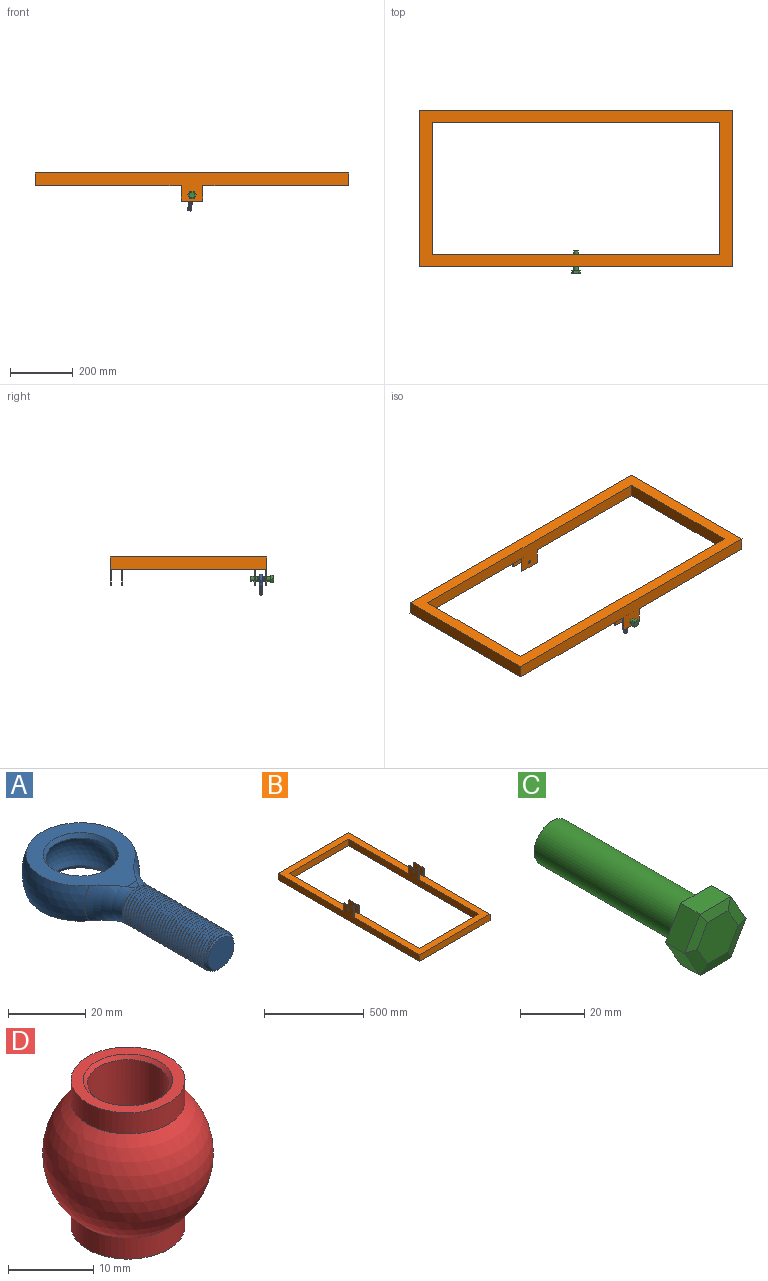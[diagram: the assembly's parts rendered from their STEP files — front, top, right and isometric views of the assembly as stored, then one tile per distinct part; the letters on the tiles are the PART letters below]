
ASSEMBLY  parts=4 mates=4
PART A: 18 faces, bbox 40.4x67.6x40.4 mm
  f0: sphere r=10mm, area 550.8mm2, adj f16,f17
  f1: sphere r=15.24mm, area 857.9mm2, adj f2,f6,f12,f14
  f2: torus R=18.29mm, axis (0,-1,0), area 150.2mm2, adj f1,f11,f12,f13,f14,f15
  f3: cone r=5.71mm half-angle=45deg, axis (0,1,0), area 26mm2, adj f4,f7,f8,f9,f10
  f4: cone r=5.71mm half-angle=45deg, axis (0,1,0), area 3.2mm2, adj f3,f5,f9,f10
  f5: cylinder r=5.71mm len=29.53mm, axis (0,1,0), area 132.5mm2, adj f4,f6,f9,f10
  f6: torus R=18.29mm, axis (0,-1,0), area 150.2mm2, adj f1,f5,f11,f12,f13,f14,f15
  f7: plane 9.53x9.53mm, normal (0,-1,0), area 71.3mm2, adj f3
  f8: bspline ~30.6x10.19mm, area 120.9mm2, adj f3,f9,f10,f11
  f9: bspline ~30.96x11.43mm, area 761.5mm2, adj f3,f4,f5,f8,f11
  f10: bspline ~30.72x11.43mm, area 760.1mm2, adj f3,f4,f5,f8,f11
  f11: plane 11.81x11.81mm, normal (0,-1,0), area 10.6mm2, adj f2,f6,f8,f9,f10
  f12: plane 33.71x29.17mm, normal (0,0,1), area 369.6mm2, adj f1,f2,f6,f13,f17
  f13: plane 4.19x2.59mm, normal (0,0.05,1), area 5mm2, adj f2,f6,f12
  f14: plane 33.71x29.17mm, normal (0,0,-1), area 370.1mm2, adj f1,f2,f6,f15,f16
  f15: plane 4.19x2.59mm, normal (0,0.05,-1), area 4.9mm2, adj f2,f6,f14
  f16: cone r=9.75mm half-angle=32deg, axis (0,0,-1), area 84.2mm2, adj f0,f14
  f17: cone r=9.75mm half-angle=32deg, axis (0,0,1), area 84.2mm2, adj f0,f12
PART B: 30 faces, bbox 500x1000x90 mm
  f0: plane 1000x500mm, normal (0,0,1), area 112760mm2, adj f1,f2,f3,f4,f5,f6,f7,f8
  f1: plane 500x40mm, normal (0,-1,0), area 20000mm2, adj f0,f2,f8,f9
  f2: plane 1000x90mm, normal (1,0,0), area 43421.5mm2, adj f0,f1,f3,f9,f14,f16,f17,f28
  f3: plane 500x40mm, normal (0,1,0), area 20000mm2, adj f0,f2,f8,f9
  f4: plane 420x40mm, normal (0,1,0), area 16800mm2, adj f0,f5,f7,f9
  f5: plane 920x90mm, normal (1,0,0), area 40221.5mm2, adj f0,f4,f6,f9,f18,f20,f21,f27
  f6: plane 420x40mm, normal (0,-1,0), area 16800mm2, adj f0,f5,f7,f9
  f7: plane 920x90mm, normal (-1,0,0), area 40221.5mm2, adj f0,f4,f6,f9,f10,f11,f13,f29
  f8: plane 1000x90mm, normal (-1,0,0), area 43421.5mm2, adj f0,f1,f3,f9,f22,f23,f25,f26
  f9: plane 1000x500mm, normal (0,0,-1), area 113600mm2, adj f1,f2,f3,f4,f5,f6,f7,f8
  f10: plane 50x3mm, normal (0,1,0), area 150mm2, adj f0,f7,f12,f13
  f11: plane 50x3mm, normal (0,-1,0), area 150mm2, adj f0,f7,f12,f13
  f12: plane 70x50mm, normal (1,0,0), area 3421.5mm2, adj f0,f10,f11,f13,f29
  f13: plane 70x3mm, normal (0,0,1), area 210mm2, adj f7,f10,f11,f12
  f14: plane 50x3mm, normal (0,1,0), area 150mm2, adj f0,f2,f15,f17
  f15: plane 70x50mm, normal (-1,0,0), area 3421.5mm2, adj f0,f14,f16,f17,f28
  f16: plane 50x3mm, normal (0,-1,0), area 150mm2, adj f0,f2,f15,f17
  f17: plane 70x3mm, normal (0,0,1), area 210mm2, adj f2,f14,f15,f16
  f18: plane 50x3mm, normal (0,1,0), area 150mm2, adj f0,f5,f19,f21
  f19: plane 70x50mm, normal (-1,0,0), area 3421.5mm2, adj f0,f18,f20,f21,f27
  f20: plane 50x3mm, normal (0,-1,0), area 150mm2, adj f0,f5,f19,f21
  f21: plane 70x3mm, normal (0,0,1), area 210mm2, adj f5,f18,f19,f20
  f22: plane 50x3mm, normal (0,1,0), area 150mm2, adj f0,f8,f24,f25
  f23: plane 50x3mm, normal (0,-1,0), area 150mm2, adj f0,f8,f24,f25
  f24: plane 70x50mm, normal (1,0,0), area 3421.5mm2, adj f0,f22,f23,f25,f26
  f25: plane 70x3mm, normal (0,0,1), area 210mm2, adj f8,f22,f23,f24
  f26: cylinder r=5mm len=10mm, axis (-1,0,0), area 94.2mm2, adj f8,f24
  f27: cylinder r=5mm len=10mm, axis (-1,0,0), area 94.2mm2, adj f5,f19
  f28: cylinder r=5mm len=10mm, axis (-1,0,0), area 94.2mm2, adj f2,f15
  f29: cylinder r=5mm len=10mm, axis (-1,0,0), area 94.2mm2, adj f7,f12
PART C: 16 faces, bbox 27x73x23.4 mm
  f0: plane 11.69x8.5mm, normal (0.87,0,-0.5), area 114.8mm2, adj f1,f5,f7,f13
  f1: plane 11.69x8.5mm, normal (0.87,0,0.5), area 114.8mm2, adj f0,f2,f7,f11
  f2: plane 13.49x8.5mm, normal (0,0,1), area 114.8mm2, adj f1,f3,f7,f9
  f3: plane 11.69x8.5mm, normal (-0.87,0,0.5), area 114.8mm2, adj f2,f4,f7,f8
  f4: plane 11.69x8.5mm, normal (-0.87,0,-0.5), area 114.8mm2, adj f3,f5,f7,f10
  f5: plane 13.49x8.5mm, normal (0,0,-1), area 114.8mm2, adj f0,f4,f7,f12
  f6: plane 18.19x15.75mm, normal (0,-1,0), area 214.9mm2, adj f8,f9,f10,f11,f12,f13
  f7: plane 26.99x23.37mm, normal (0,1,0), area 275.1mm2, adj f0,f1,f2,f3,f4,f5,f14
  f8: plane 11.69x8.95mm, normal (-0.22,-0.97,0.13), area 44.5mm2, adj f3,f6,f9,f10
  f9: plane 13.49x3.81mm, normal (0,-0.97,0.26), area 44.5mm2, adj f2,f6,f8,f11
  f10: plane 11.69x8.95mm, normal (-0.22,-0.97,-0.13), area 44.5mm2, adj f4,f6,f8,f12
  f11: plane 11.69x8.95mm, normal (0.22,-0.97,0.13), area 44.5mm2, adj f1,f6,f9,f13
  f12: plane 13.49x3.81mm, normal (0,-0.97,-0.26), area 44.5mm2, adj f5,f6,f10,f13
  f13: plane 11.69x8.95mm, normal (0.22,-0.97,-0.13), area 44.5mm2, adj f0,f6,f11,f12
  f14: cylinder r=7.94mm len=63.5mm, axis (0,-1,0), area 3166.9mm2, adj f7,f15
  f15: plane 15.88x15.88mm, normal (0,1,0), area 197.9mm2, adj f14
PART D: 8 faces, bbox 20x20x21 mm
  f0: cone r=4.76mm half-angle=45deg, axis (0,0,1), area 21.2mm2, adj f2,f6
  f1: cone r=4.76mm half-angle=45deg, axis (0,0,-1), area 21.2mm2, adj f2,f7
  f2: cylinder r=4.76mm len=20mm, axis (0,0,1), area 598.5mm2, adj f0,f1
  f3: cylinder r=6.67mm len=13.34mm, axis (0,0,-1), area 126.6mm2, adj f5,f7
  f4: cylinder r=6.67mm len=13.34mm, axis (0,0,-1), area 126.6mm2, adj f5,f6
  f5: sphere r=10mm, area 936.9mm2, adj f3,f4
  f6: plane 13.34x13.34mm, normal (0,0,1), area 53.4mm2, adj f0,f4
  f7: plane 13.34x13.34mm, normal (0,0,-1), area 53.4mm2, adj f1,f3
PLACE A rot(axis=(-0.06,-0.71,-0.71),172.9deg) t=(-378.01,95.36,-274.39)mm
PLACE B rot(axis=(-0.71,-0.71,0),180deg) t=(-874.34,576.79,-183.76)mm
PLACE C t=(-374.34,63.61,-253.76)mm
PLACE D rot(axis=(-1,0,0),90deg) t=(-374.34,95.36,-232.8)mm
MATE parallel B.f24 <-> A.f12  axis (0,1,0) through (-374.34,79.79,-248.64)mm
MATE ball A.f16 <-> D.f0  axis (0,1,0) through (-374.34,95.36,-253.76)mm
MATE fastened D.f0 <-> C.f14  axis (0,1,0) through (-374.34,95.36,-253.76)mm
MATE slider B.f26 <-> C.f14  axis (0,-1,0) through (-374.34,76.79,-253.76)mm
